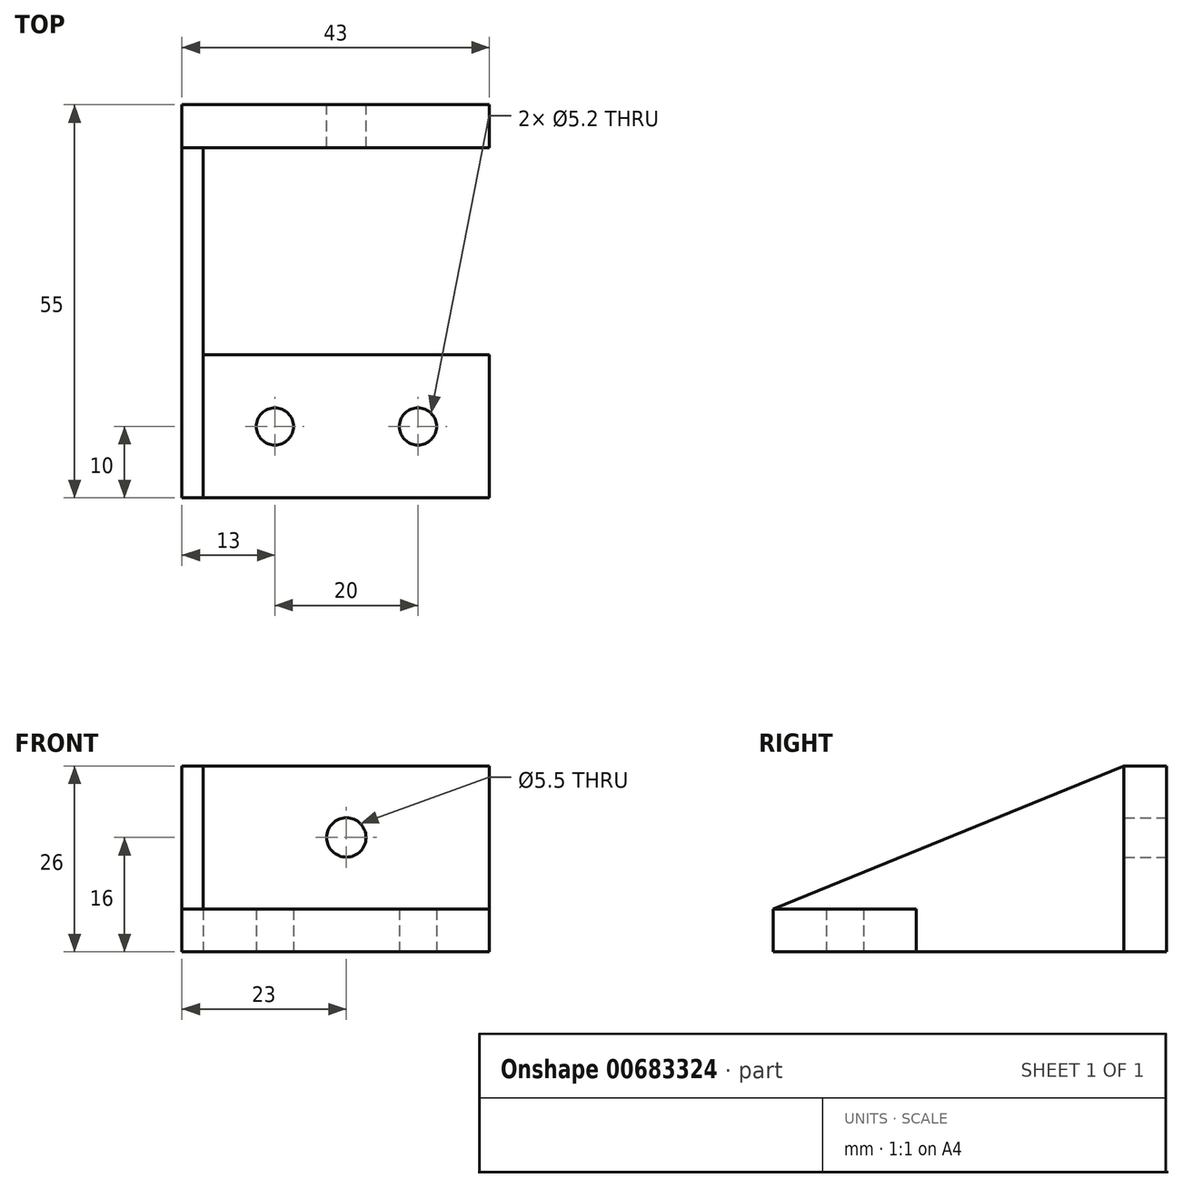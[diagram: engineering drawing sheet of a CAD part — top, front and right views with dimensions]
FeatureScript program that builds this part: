
annotation { "Feature Type Name" : "Feature", "Feature Type Description" : "" }
export const myFeature = defineFeature(function(context is Context, id is Id, definition is map)
    precondition{}
    {
        {
            var Q0;
            Q0=qCreatedBy(makeId("Top.planeOp"),FACE);
            var sketch = newSketch(context, id + "F0", { "sketchPlane" : qUnion([Q0])});
            skLineSegment(sketch, "E0.bottom", {"start": v(20, 10) * mm, "end": v(-20, 10) * mm});
            skLineSegment(sketch, "E0.top", {"start": v(20, -10) * mm, "end": v(-20, -10) * mm});
            skLineSegment(sketch, "E0.left", {"start": v(20, 10) * mm, "end": v(20, -10) * mm});
            skLineSegment(sketch, "E0.right", {"start": v(-20, 10) * mm, "end": v(-20, -10) * mm});
            skPoint(sketch, "E0.middle", {"position": v(0, 0) * mm});
            skLineSegment(sketch, "E1", {"start": v(0, -10) * mm, "end": v(0, 10) * mm, "construction": true});
            skLineSegment(sketch, "E2", {"start": v(0, 10) * mm, "end": v(20, 10) * mm, "construction": true});
            skLineSegment(sketch, "E3", {"start": v(10, 10) * mm, "end": v(10, -10) * mm, "construction": true});
            skLineSegment(sketch, "E4", {"start": v(-20, 10) * mm, "end": v(0, 10) * mm, "construction": true});
            skLineSegment(sketch, "E5", {"start": v(-10, 10) * mm, "end": v(-10, -10) * mm, "construction": true});
            skCircle(sketch, "E6", {"center": v(-10, 0) * mm, "radius": 2.6 * mm});
            skCircle(sketch, "E7", {"center": v(10, 0) * mm, "radius": 2.6 * mm});
            skLineSegment(sketch, "E8.bottom", {"start": v(-20, 10) * mm, "end": v(20, 10) * mm});
            skLineSegment(sketch, "E8.top", {"start": v(-20, 45) * mm, "end": v(20, 45) * mm});
            skLineSegment(sketch, "E8.left", {"start": v(-20, 10) * mm, "end": v(-20, 45) * mm});
            skLineSegment(sketch, "E8.right", {"start": v(20, 10) * mm, "end": v(20, 45) * mm});
            skLineSegment(sketch, "E9.top", {"start": v(-20, 39) * mm, "end": v(20, 39) * mm});
            skLineSegment(sketch, "E9.left", {"start": v(-20, 45) * mm, "end": v(-20, 39) * mm});
            skLineSegment(sketch, "E9.right", {"start": v(20, 45) * mm, "end": v(20, 39) * mm});
            skSolve(sketch);
        }
        {
            var Q0;
            Q0=makeQuery(id+"F0.imprint","IMPRINT",FACE,{"disambiguationData":[TD([[makeQuery(id+"F0.imprint","IMPRINT",EDGE,{"derivedFrom":sQuery(id+"F0.wireOp",EDGE,"E8.bottom")}),1.0]])]});
            var Q1;
            Q1=makeQuery(id+"F0.imprint","IMPRINT",FACE,{"disambiguationData":[TD([[makeQuery(id+"F0.imprint","IMPRINT",EDGE,{"derivedFrom":sQuery(id+"F0.wireOp",EDGE,"E0.top")}),-1.0]])]});
            extrude(context, id + "F1", {"entities" : qUnion([Q0, Q1]), "depth" : 6 * mm, "offsetDistance" : 25 * mm});
        }
        {
            var Q0;
            Q0=makeQuery(id+"F0.imprint","IMPRINT",FACE,{"disambiguationData":[TD([[makeQuery(id+"F0.imprint","IMPRINT",EDGE,{"derivedFrom":sQuery(id+"F0.wireOp",EDGE,"E8.top")}),-1.0]])]});
            extrude(context, id + "F2", {"entities" : qUnion([Q0]), "operationType" : NewBodyOperationType.ADD, "depth" : 26 * mm, "offsetDistance" : 25 * mm});
        }
        {
            var Q0;
            Q0=makeQuery(id+"F2.boolean.opBoolean","MERGE",FACE,{"derivedFrom":[makeQuery(id+"F1.opExtrude","SWEPT_FACE",FACE,{"disambiguationData":[OSD([sQuery(id+"F0.wireOp",EDGE,"E0.right"),sQuery(id+"F0.wireOp",EDGE,"E8.left")])]}),makeQuery(id+"F2.opExtrude","SWEPT_FACE",FACE,{"disambiguationData":[OSD([sQuery(id+"F0.wireOp",EDGE,"E9.left")])]})]});
            var sketch = newSketch(context, id + "F3", { "sketchPlane" : qUnion([Q0])});
            skLineSegment(sketch, "E10", {"start": v(10, 6) * mm, "end": v(-39, 26) * mm});
            skLineSegment(sketch, "E11", {"start": v(-39, 26) * mm, "end": v(-45, 26) * mm});
            skLineSegment(sketch, "E12", {"start": v(-45, 26) * mm, "end": v(-45, 0) * mm});
            skLineSegment(sketch, "E13", {"start": v(-45, 0) * mm, "end": v(10, 0) * mm});
            skLineSegment(sketch, "E14", {"start": v(10, 0) * mm, "end": v(10, 6) * mm});
            skSolve(sketch);
        }
        {
            var Q0;
            Q0 = qSketchRegion(id + "F3", true);
            extrude(context, id + "F4", {"entities" : qUnion([Q0]), "operationType" : NewBodyOperationType.ADD, "depth" : 3 * mm, "offsetDistance" : 25 * mm});
        }
        {
            var Q0;
            {var subQ0=sQuery(id+"F3.wireOp",EDGE,"E12");Q0=makeQuery(id+"F8NfSc3ifBcihHt_1.1.F4.boolean.opBoolean","MERGE",FACE,{"derivedFrom":[makeQuery(id+"F4.boolean.opBoolean","MERGE",FACE,{"derivedFrom":[makeQuery(id+"F2.opExtrude","SWEPT_FACE",FACE,{"disambiguationData":[OSD([sQuery(id+"F0.wireOp",EDGE,"E8.top")])]}),makeQuery(id+"F4.opExtrude","SWEPT_FACE",FACE,{"disambiguationData":[OSD([subQ0])]})]}),makeQuery(id+"F8NfSc3ifBcihHt_1.1.F4.opExtrude","SWEPT_FACE",FACE,{"disambiguationData":[OSD([subQ0])]})]});}
            var sketch = newSketch(context, id + "F5", { "sketchPlane" : qUnion([Q0])});
            skLineSegment(sketch, "E15", {"start": v(0, 26) * mm, "end": v(0, 16) * mm});
            skCircle(sketch, "E16", {"center": v(0, 16) * mm, "radius": 2.75 * mm});
            skSolve(sketch);
        }
        {
            var Q0;
            Q0 = qSketchRegion(id + "F5", true);
            extrude(context, id + "F6", {"entities" : qUnion([Q0]), "operationType" : NewBodyOperationType.REMOVE, "oppositeDirection" : true, "depth" : 25 * mm, "offsetDistance" : 25 * mm});
        }
    });
